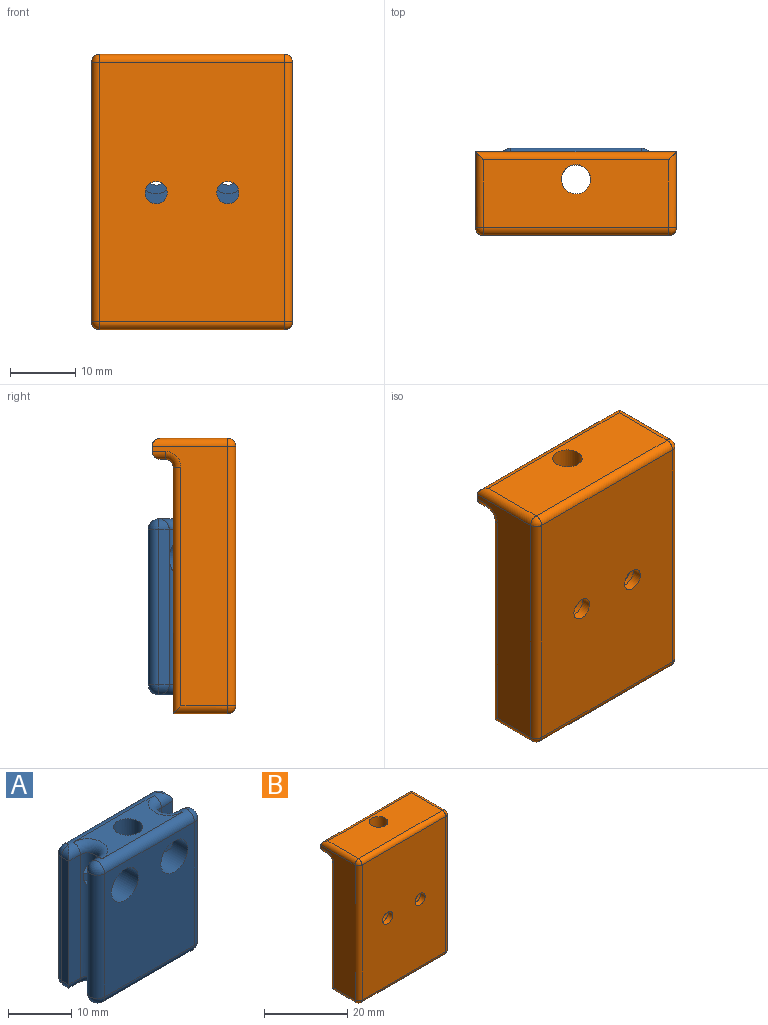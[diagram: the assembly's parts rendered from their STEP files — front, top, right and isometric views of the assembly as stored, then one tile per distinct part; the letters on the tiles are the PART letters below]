
ASSEMBLY  parts=2 mates=1
PART A: 51 faces, bbox 23.2x9.6x27 mm
  f0: plane 6.53x6.4mm, normal (0,0,-1), area 19.8mm2, adj f1,f2,f28,f45,f46
  f1: cylinder r=1.6mm len=20mm, axis (1,0,0), area 52.7mm2, adj f0,f5,f11,f13,f16,f20,f21,f27
  f2: cylinder r=1.6mm len=23.22mm, axis (1,0,0), area 57.9mm2, adj f0,f6,f8,f10,f16,f26,f27,f28
  f3: cylinder r=1.6mm len=23.8mm, axis (0,0,-1), area 104.7mm2, adj f5,f6,f22,f28,f40
  f4: cylinder r=1.6mm len=23.8mm, axis (0,0,-1), area 104.8mm2, adj f10,f11,f23,f27,f39
  f5: plane 23.8x1mm, normal (0,1,0), area 23.8mm2, adj f1,f3,f14,f18
  f6: plane 23.8x2.6mm, normal (0,-1,0), area 61.9mm2, adj f2,f3,f7,f29
  f7: plane 23.8x1.6mm, normal (1,0,0), area 38.1mm2, adj f6,f32,f33,f36
  f8: plane 23.8x20.02mm, normal (0,1,0), area 458.3mm2, adj f2,f25,f29,f36,f37,f41
  f9: plane 23.8x1.6mm, normal (-1,0,0), area 38.1mm2, adj f10,f24,f25,f26
  f10: plane 23.8x2.6mm, normal (0,-1,0), area 61.9mm2, adj f2,f4,f9,f29
  f11: plane 23.8x1mm, normal (0,1,0), area 23.8mm2, adj f1,f4,f12,f18
  f12: cylinder r=1.6mm len=23.8mm, axis (0,0,-1), area 119.6mm2, adj f11,f13,f19,f20
  f13: plane 23.8x20mm, normal (0,-1,0), area 419.5mm2, adj f1,f12,f14,f18,f39,f40
  f14: cylinder r=1.6mm len=23.8mm, axis (0,0,-1), area 119.6mm2, adj f5,f13,f17,f21
  f15: plane 18.02x6.4mm, normal (0,0,1), area 67.3mm2, adj f18,f22,f23,f29,f50
  f16: plane 6.53x6.4mm, normal (0,0,-1), area 19.8mm2, adj f1,f2,f27,f43,f48
  f17: sphere r=1.6mm, area 8mm2, adj f14,f18
  f18: cylinder r=1.6mm len=20mm, axis (-1,0,0), area 55.3mm2, adj f5,f11,f13,f15,f17,f19,f22,f23
  f19: sphere r=1.6mm, area 8mm2, adj f12,f18
  f20: sphere r=1.6mm, area 8mm2, adj f1,f12
  f21: sphere r=1.6mm, area 8mm2, adj f1,f14
  f22: torus R=3.2mm, axis (0,0,1), area 17.2mm2, adj f3,f15,f18,f29
  f23: torus R=3.2mm, axis (0,0,1), area 17.2mm2, adj f4,f15,f18,f29
  f24: cylinder r=1.6mm len=1.6mm, axis (0,1,0), area 2.6mm2, adj f9,f29,f30
  f25: cylinder r=1.6mm len=23.8mm, axis (0,0,-1), area 59.8mm2, adj f8,f9,f30,f31
  f26: cylinder r=1.6mm len=1.6mm, axis (0,-1,0), area 2.6mm2, adj f2,f9,f31
  f27: torus R=3.2mm, axis (0,0,1), area 17.2mm2, adj f1,f2,f4,f16
  f28: torus R=3.2mm, axis (0,0,1), area 17.2mm2, adj f0,f1,f2,f3
  f29: cylinder r=1.6mm len=23.22mm, axis (-1,0,0), area 60.5mm2, adj f6,f8,f10,f15,f22,f23,f24,f30
  f30: sphere r=1.6mm, area 4mm2, adj f24,f25,f29
  f31: sphere r=1.6mm, area 4mm2, adj f2,f25,f26
  f32: cylinder r=1.6mm len=1.6mm, axis (0,-1,0), area 2.6mm2, adj f7,f29,f34
  f33: cylinder r=1.6mm len=1.6mm, axis (0,1,0), area 2.6mm2, adj f2,f7,f35
  f34: sphere r=1.6mm, area 4mm2, adj f29,f32,f36
  f35: sphere r=1.6mm, area 4mm2, adj f2,f33,f36
  f36: cylinder r=1.6mm len=23.8mm, axis (0,0,1), area 59.8mm2, adj f7,f8,f34,f35
  f37: cylinder r=1.7mm len=3.4mm, axis (0,-1,0), area 16mm2, adj f8,f38
  f38: plane 6x6mm, normal (0,-1,0), area 19.2mm2, adj f37,f39
  f39: cylinder r=3mm len=8.1mm, axis (0,-1,0), area 139.4mm2, adj f4,f13,f38
  f40: cylinder r=3mm len=8.1mm, axis (0,-1,0), area 139.4mm2, adj f3,f13,f42
  f41: cylinder r=1.7mm len=3.4mm, axis (0,-1,0), area 16mm2, adj f8,f42
  f42: plane 6x6mm, normal (0,-1,0), area 19.2mm2, adj f40,f41
  f43: plane 4.01x3.76mm, normal (0.87,-0.5,0), area 17.3mm2, adj f2,f16,f44,f48,f49
  f44: plane 4.33x3.9mm, normal (0,-1,0), area 16.9mm2, adj f2,f43,f45,f49
  f45: plane 4.01x3.76mm, normal (-0.87,-0.5,0), area 17.3mm2, adj f0,f2,f44,f46,f49
  f46: plane 4.01x3.76mm, normal (-0.87,0.5,0), area 17.3mm2, adj f0,f1,f45,f47,f49
  f47: plane 4.33x3.9mm, normal (0,1,0), area 16.9mm2, adj f1,f46,f48,f49
  f48: plane 4.01x3.76mm, normal (0.87,0.5,0), area 17.3mm2, adj f1,f16,f43,f47,f49
  f49: plane 8.66x7.5mm, normal (0,0,-1), area 32.8mm2, adj f43,f44,f45,f46,f47,f48,f50
  f50: cylinder r=2.25mm len=23mm, axis (0,0,-1), area 325.2mm2, adj f15,f49
PART B: 52 faces, bbox 30.8x12.8x42.2 mm
  f0: plane 39.8x28.4mm, normal (0,-1,0), area 1112.2mm2, adj f13,f16,f34,f35,f43,f44
  f1: plane 39.8x11.6mm, normal (1,0,0), area 291.3mm2, adj f19,f36,f44,f45,f48,f49,f50
  f2: plane 37.8x5.19mm, normal (0,1,0), area 196.2mm2, adj f3,f12,f46,f50
  f3: cylinder r=1mm len=37.8mm, axis (0,0,-1), area 118.5mm2, adj f2,f4,f12,f42
  f4: plane 37.8x1mm, normal (0,-1,0), area 37.7mm2, adj f3,f5,f12,f38
  f5: cylinder r=2.2mm len=37.8mm, axis (0,0,-1), area 261.3mm2, adj f4,f6,f12,f32
  f6: plane 37.8x20mm, normal (0,1,0), area 699.5mm2, adj f5,f7,f12,f15,f18,f26
  f7: cylinder r=2.2mm len=37.8mm, axis (0,0,-1), area 261.3mm2, adj f6,f8,f12,f24
  f8: plane 37.8x1mm, normal (0,-1,0), area 37.7mm2, adj f7,f9,f12,f22
  f9: cylinder r=1mm len=37.8mm, axis (0,0,-1), area 118.5mm2, adj f8,f10,f12,f23
  f10: plane 37.8x5.19mm, normal (0,1,0), area 196.2mm2, adj f9,f12,f25,f28
  f11: plane 39.8x11.6mm, normal (-1,0,0), area 291.3mm2, adj f19,f27,f28,f31,f33,f34,f37
  f12: plane 28.4x8.4mm, normal (0,0,-1), area 102.5mm2, adj f2,f3,f4,f5,f6,f7,f8,f9
  f13: cylinder r=1.7mm len=3.4mm, axis (0,1,0), area 16mm2, adj f0,f14
  f14: plane 6x6mm, normal (0,1,0), area 19.2mm2, adj f13,f15
  f15: cylinder r=3mm len=6mm, axis (0,1,0), area 32mm2, adj f6,f14
  f16: cylinder r=1.7mm len=3.4mm, axis (0,1,0), area 16mm2, adj f0,f17
  f17: plane 6x6mm, normal (0,1,0), area 19.2mm2, adj f16,f18
  f18: cylinder r=3mm len=6mm, axis (0,1,0), area 32mm2, adj f6,f17
  f19: plane 30.8x0.8mm, normal (0,1,0), area 24.6mm2, adj f1,f11,f30,f41
  f20: plane 28.4x10.4mm, normal (0,0,1), area 279.5mm2, adj f27,f30,f35,f36,f51
  f21: plane 28.4x7.2mm, normal (0,0,-1), area 114mm2, adj f22,f23,f24,f25,f26,f32,f37,f38
  f22: cylinder r=1.2mm len=1.2mm, axis (-1,0,0), area 1.9mm2, adj f8,f21,f23,f24
  f23: torus R=2.2mm, axis (0,0,1), area 8.5mm2, adj f9,f21,f22,f25
  f24: torus R=1mm, axis (0,0,1), area 10.4mm2, adj f7,f21,f22,f26
  f25: cylinder r=1.2mm len=5.19mm, axis (1,0,0), area 9.8mm2, adj f10,f21,f23,f31
  f26: cylinder r=1.2mm len=20mm, axis (1,0,0), area 37.7mm2, adj f6,f21,f24,f32
  f27: cylinder r=1.2mm len=11.6mm, axis (0,1,0), area 21mm2, adj f11,f20,f29,f30
  f28: cylinder r=1.2mm len=37.8mm, axis (0,0,-1), area 70.4mm2, adj f10,f11,f31,f33
  f29: sphere r=1.2mm, area 2.3mm2, adj f27,f34,f35
  f30: cylinder r=1.2mm len=30.8mm, axis (1,0,0), area 56.4mm2, adj f19,f20,f27,f36
  f31: torus R=2.4mm, axis (1,0,0), area 4.8mm2, adj f11,f25,f28,f37
  f32: torus R=1mm, axis (0,0,1), area 10.4mm2, adj f5,f21,f26,f38
  f33: cylinder r=1.2mm len=8.4mm, axis (0,-1,0), area 15mm2, adj f11,f12,f28,f39
  f34: cylinder r=1.2mm len=39.8mm, axis (0,0,-1), area 75mm2, adj f0,f11,f29,f39
  f35: cylinder r=1.2mm len=28.4mm, axis (-1,0,0), area 53.5mm2, adj f0,f20,f29,f40
  f36: cylinder r=1.2mm len=11.6mm, axis (0,-1,0), area 21mm2, adj f1,f20,f30,f40
  f37: cylinder r=1.2mm len=2mm, axis (0,-1,0), area 2.9mm2, adj f11,f21,f31,f41
  f38: cylinder r=1.2mm len=1.2mm, axis (-1,0,0), area 1.9mm2, adj f4,f21,f32,f42
  f39: sphere r=1.2mm, area 2.3mm2, adj f33,f34,f43
  f40: sphere r=1.2mm, area 2.3mm2, adj f35,f36,f44
  f41: cylinder r=1.2mm len=30.8mm, axis (-1,0,0), area 56.4mm2, adj f19,f21,f37,f45
  f42: torus R=2.2mm, axis (0,0,1), area 8.5mm2, adj f3,f21,f38,f46
  f43: cylinder r=1.2mm len=28.4mm, axis (1,0,0), area 53.5mm2, adj f0,f12,f39,f47
  f44: cylinder r=1.2mm len=39.8mm, axis (0,0,1), area 75mm2, adj f0,f1,f40,f47
  f45: cylinder r=1.2mm len=2mm, axis (0,1,0), area 2.9mm2, adj f1,f21,f41,f48
  f46: cylinder r=1.2mm len=5.19mm, axis (1,0,0), area 9.8mm2, adj f2,f21,f42,f48
  f47: sphere r=1.2mm, area 2.3mm2, adj f43,f44,f49
  f48: torus R=2.4mm, axis (1,0,0), area 4.8mm2, adj f1,f45,f46,f50
  f49: cylinder r=1.2mm len=8.4mm, axis (0,1,0), area 15mm2, adj f1,f12,f47,f50
  f50: cylinder r=1.2mm len=37.8mm, axis (0,0,-1), area 70.4mm2, adj f1,f2,f48,f49
  f51: cylinder r=2.25mm len=4.5mm, axis (0,0,-1), area 45.2mm2, adj f20,f21
PLACE A t=(-21.41,-10.52,-30.34)mm
PLACE B rot(axis=(0.3,-0.04,-0.95),0deg) t=(-21.41,-10.52,-27.19)mm
MATE slider A.f50 <-> B.f51  axis (0,0,-1) through (-21.41,-9.39,-16.84)mm
